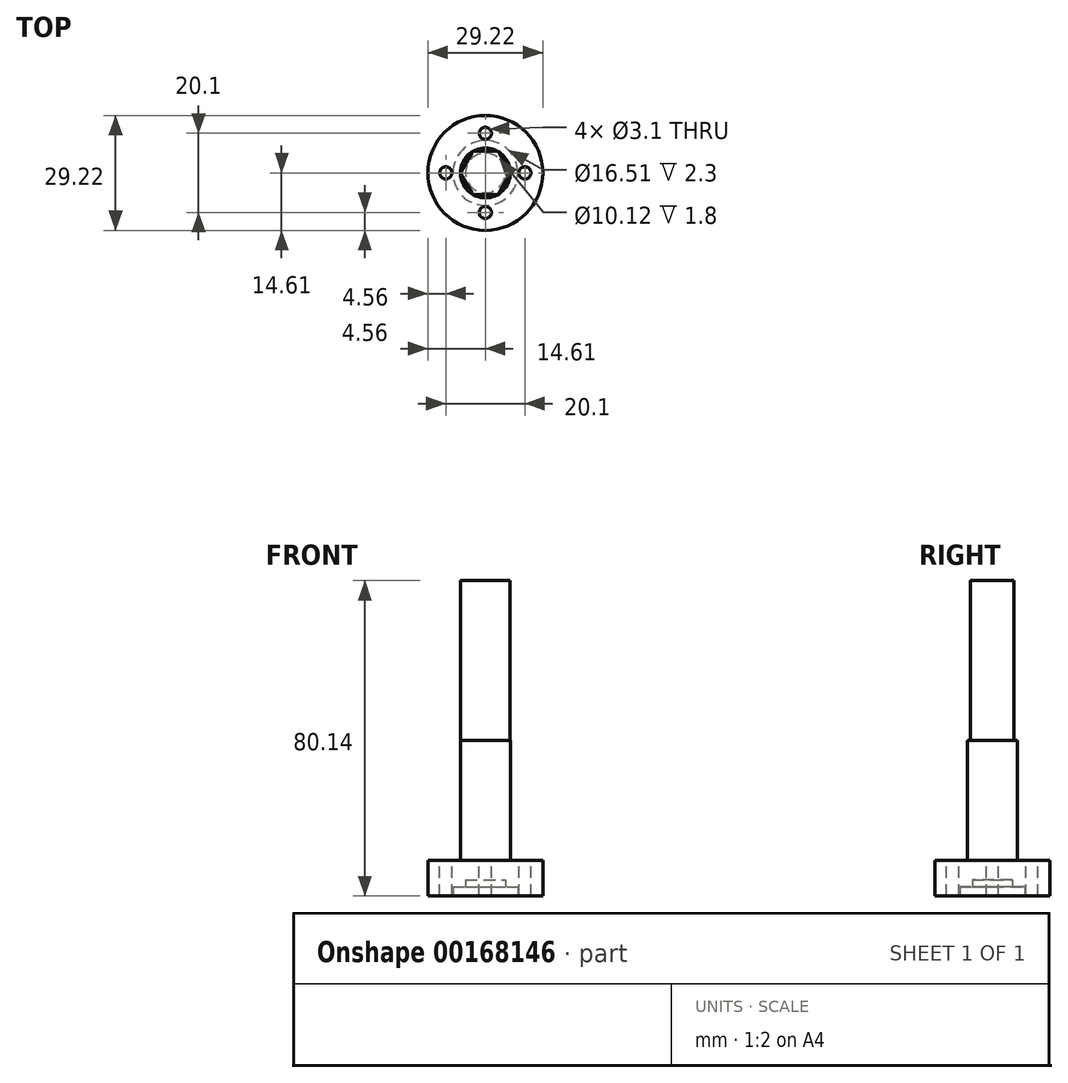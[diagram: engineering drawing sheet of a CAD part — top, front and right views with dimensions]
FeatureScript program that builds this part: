
annotation { "Feature Type Name" : "Feature", "Feature Type Description" : "" }
export const myFeature = defineFeature(function(context is Context, id is Id, definition is map)
    precondition{}
    {
        {
            var Q0;
            Q0=qCreatedBy(makeId("Top.planeOp"),FACE);
            var sketch = newSketch(context, id + "F0", { "sketchPlane" : qUnion([Q0])});
            skCircle(sketch, "E0", {"center": v(0, 0) * mm, "radius": 14.6 * mm});
            skSolve(sketch);
        }
        {
            var Q0;
            Q0=makeQuery(id+"F0.imprint","IMPRINT",FACE,{"disambiguationData":[TD([[makeQuery(id+"F0.imprint","IMPRINT",EDGE,{"derivedFrom":sQuery(id+"F0.wireOp",EDGE,"E0")}),1.0]])]});
            extrude(context, id + "F1", {"entities" : qUnion([Q0]), "depth" : 9.02 * mm});
        }
        {
            var Q0;
            Q0=makeQuery(id+"F1.opExtrude","CAP_FACE",FACE,{"disambiguationData":[OSD([sQuery(id+"F0.wireOp",EDGE,"E0")])],"isStart":false});
            var sketch = newSketch(context, id + "F2", { "sketchPlane" : qUnion([Q0])});
            skCircle(sketch, "E1", {"center": v(0, 0) * mm, "radius": 6.35 * mm});
            skSolve(sketch);
        }
        {
            var Q0;
            Q0=qSketchRegion(id+"F2",true);
            extrude(context, id + "F3", {"entities" : qUnion([Q0]), "operationType" : NewBodyOperationType.ADD, "depth" : 30.48 * mm});
        }
        {
            var Q0;
            Q0=makeQuery(id+"F3.opExtrude","CAP_FACE",FACE,{"disambiguationData":[OSD([sQuery(id+"F2.wireOp",EDGE,"E1")])],"isStart":false});
            var sketch = newSketch(context, id + "F4", { "sketchPlane" : qUnion([Q0])});
            skCircle(sketch, "E2.cCircle", {"center": v(0, 0) * mm, "radius": 5.54 * mm, "construction": true});
            skLineSegment(sketch, "E2.0", {"start": v(6.17, -0.38) * mm, "end": v(3.42, -5.16) * mm});
            skLineSegment(sketch, "E2.1", {"start": v(2.76, -5.54) * mm, "end": v(-2.76, -5.54) * mm});
            skLineSegment(sketch, "E2.2", {"start": v(-3.42, -5.16) * mm, "end": v(-6.17, -0.38) * mm});
            skLineSegment(sketch, "E2.3", {"start": v(-6.17, 0.38) * mm, "end": v(-3.42, 5.16) * mm});
            skLineSegment(sketch, "E2.4", {"start": v(-2.76, 5.54) * mm, "end": v(2.76, 5.54) * mm});
            skLineSegment(sketch, "E2.5", {"start": v(3.42, 5.16) * mm, "end": v(6.17, 0.38) * mm});
            skPoint(sketch, "E2.0.midPoint", {"position": v(4.8, -2.77) * mm});
            skPoint(sketch, "E3.visualSharp", {"position": v(-3.2, 5.54) * mm});
            skArc(sketch, "E3.filletArc", {"start": v(-2.76, 5.54) * mm, "mid": v(-3.14, 5.44) * mm, "end": v(-3.42, 5.16) * mm});
            skPoint(sketch, "E4.visualSharp", {"position": v(3.2, 5.54) * mm});
            skArc(sketch, "E4.filletArc", {"start": v(3.42, 5.16) * mm, "mid": v(3.14, 5.44) * mm, "end": v(2.76, 5.54) * mm});
            skPoint(sketch, "E5.visualSharp", {"position": v(6.4, 0) * mm});
            skArc(sketch, "E5.filletArc", {"start": v(6.17, -0.38) * mm, "mid": v(6.28, 0) * mm, "end": v(6.17, 0.38) * mm});
            skPoint(sketch, "E6.visualSharp", {"position": v(3.2, -5.54) * mm});
            skArc(sketch, "E6.filletArc", {"start": v(2.76, -5.54) * mm, "mid": v(3.14, -5.44) * mm, "end": v(3.42, -5.16) * mm});
            skPoint(sketch, "E7.visualSharp", {"position": v(-3.2, -5.54) * mm});
            skArc(sketch, "E7.filletArc", {"start": v(-3.42, -5.16) * mm, "mid": v(-3.14, -5.44) * mm, "end": v(-2.76, -5.54) * mm});
            skPoint(sketch, "E8.visualSharp", {"position": v(-6.4, 0) * mm});
            skArc(sketch, "E8.filletArc", {"start": v(-6.17, 0.38) * mm, "mid": v(-6.28, 0) * mm, "end": v(-6.17, -0.38) * mm});
            skSolve(sketch);
        }
        {
            var Q0;
            Q0=makeQuery(id+"F4.imprint","IMPRINT",FACE,{"disambiguationData":[TD([[makeQuery(id+"F4.imprint","IMPRINT",EDGE,{"derivedFrom":sQuery(id+"F4.wireOp",EDGE,"E2.0")}),-1.0]])]});
            extrude(context, id + "F5", {"entities" : qUnion([Q0]), "operationType" : NewBodyOperationType.ADD, "depth" : 40.64 * mm});
        }
        {
            var Q0;
            Q0=makeQuery(id+"F1.opExtrude","CAP_FACE",FACE,{"disambiguationData":[OSD([sQuery(id+"F0.wireOp",EDGE,"E0")])],"isStart":true});
            var sketch = newSketch(context, id + "F6", { "sketchPlane" : qUnion([Q0])});
            skCircle(sketch, "E9", {"center": v(0, 0) * mm, "radius": 8.26 * mm});
            skSolve(sketch);
        }
        {
            var Q0;
            Q0=qSketchRegion(id+"F6",true);
            extrude(context, id + "F7", {"entities" : qUnion([Q0]), "operationType" : NewBodyOperationType.REMOVE, "oppositeDirection" : true, "depth" : 2.3 * mm});
        }
        {
            var Q0;
            Q0=makeQuery(id+"F1.opExtrude","CAP_FACE",FACE,{"disambiguationData":[OSD([sQuery(id+"F0.wireOp",EDGE,"E0")])],"isStart":true});
            var sketch = newSketch(context, id + "F8", { "sketchPlane" : qUnion([Q0])});
            skCircle(sketch, "E10", {"center": v(0, 0) * mm, "radius": 5.06 * mm});
            skSolve(sketch);
        }
        {
            var Q0;
            Q0=qSketchRegion(id+"F8",true);
            extrude(context, id + "F9", {"entities" : qUnion([Q0]), "operationType" : NewBodyOperationType.REMOVE, "oppositeDirection" : true, "depth" : 4.1 * mm});
        }
        {
            var Q0;
            Q0=makeQuery(id+"F1.opExtrude","CAP_FACE",FACE,{"disambiguationData":[OSD([sQuery(id+"F0.wireOp",EDGE,"E0")])],"isStart":false});
            var sketch = newSketch(context, id + "F10", { "sketchPlane" : qUnion([Q0])});
            skPoint(sketch, "E11", {"position": v(-10.05, 0) * mm});
            skPoint(sketch, "E12", {"position": v(0, 10.05) * mm});
            skPoint(sketch, "E13", {"position": v(10.05, 0) * mm});
            skPoint(sketch, "E14", {"position": v(0, -10.05) * mm});
            skCircle(sketch, "E15", {"center": v(0, 0) * mm, "radius": 10.05 * mm, "construction": true});
            skSolve(sketch);
        }
        {
            var Q0;
            Q0=sQuery(id+"F10.wireOp",VERTEX,"E14");
            var Q1;
            Q1=sQuery(id+"F10.wireOp",VERTEX,"E11");
            var Q2;
            Q2=sQuery(id+"F10.wireOp",VERTEX,"E12");
            var Q3;
            Q3=sQuery(id+"F10.wireOp",VERTEX,"E13");
            var Q4;
            Q4=makeQuery(id+"F1.opExtrude","SWEPT_BODY",BODY,{"disambiguationData":[OSD([sQuery(id+"F0.wireOp",EDGE,"E0")])]});
            hole(context, id + "F11", {"style" : HoleStyle.SIMPLE, "endStyle" : HoleEndStyle.THROUGH, "holeDiameter" : 3.1 * mm, "locations" : qUnion([Q0, Q1, Q2, Q3]), "scope" : qUnion([Q4]), "isTappedThrough" : true});
        }
    });
